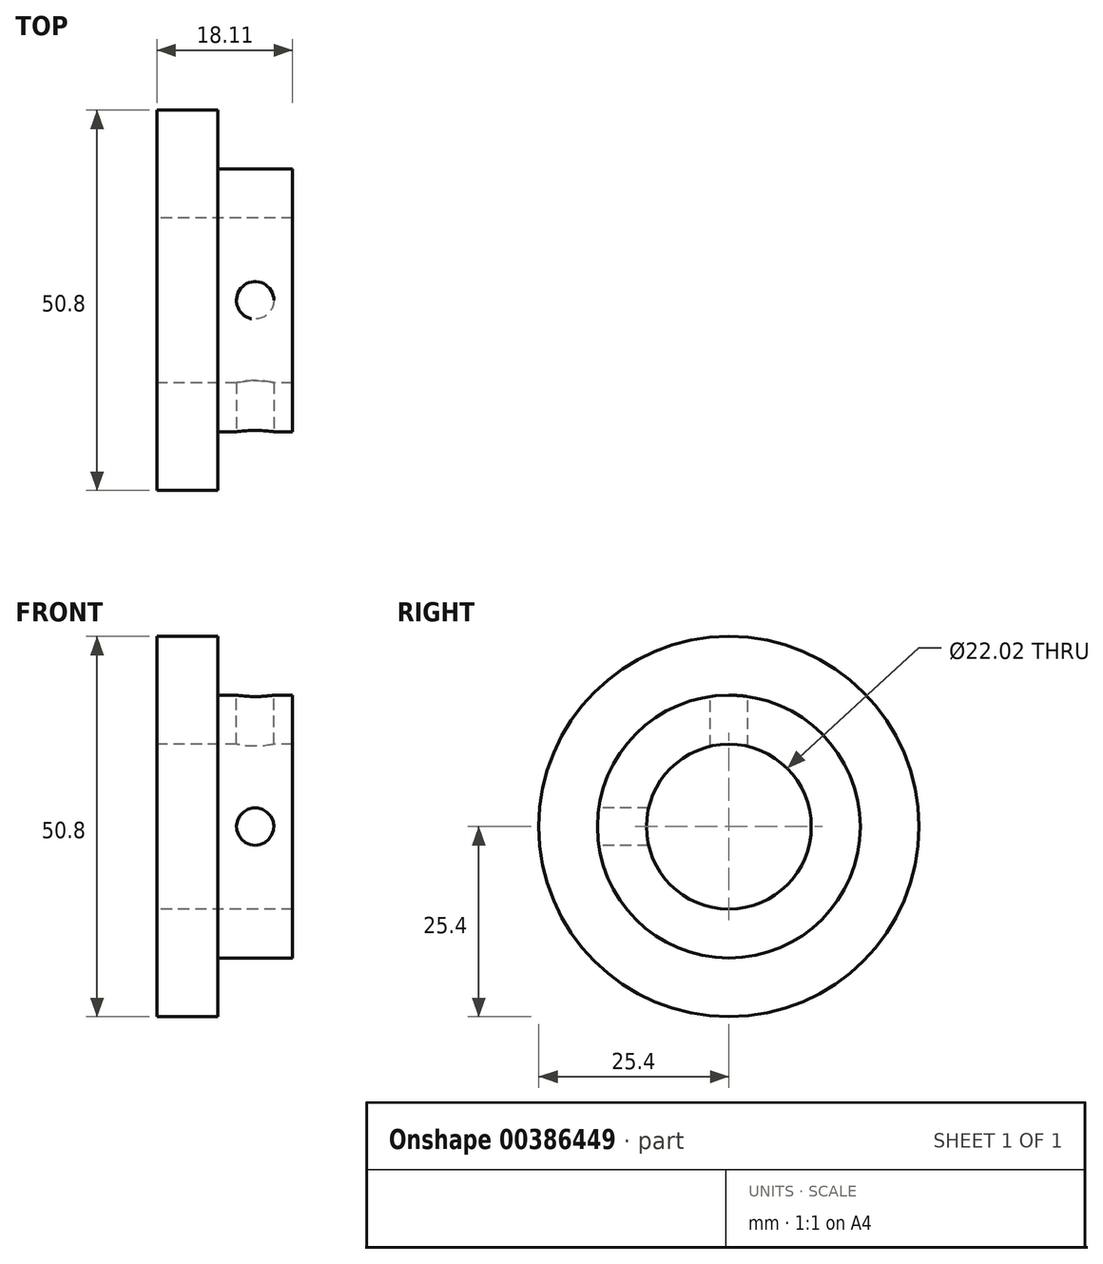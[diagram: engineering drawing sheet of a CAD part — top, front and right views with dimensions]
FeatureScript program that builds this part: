
annotation { "Feature Type Name" : "Feature", "Feature Type Description" : "" }
export const myFeature = defineFeature(function(context is Context, id is Id, definition is map)
    precondition{}
    {
        {
            var Q0;
            Q0=qCreatedBy(makeId("Front.planeOp"),FACE);
            var sketch = newSketch(context, id + "F0", { "sketchPlane" : qUnion([Q0])});
            skLineSegment(sketch, "E0", {"start": v(0, 0) * mm, "end": v(24.47, 0) * mm, "construction": true});
            skLineSegment(sketch, "E1", {"start": v(0, 11.01) * mm, "end": v(18.11, 11.01) * mm});
            skLineSegment(sketch, "E2", {"start": v(18.11, 11.01) * mm, "end": v(18.11, 17.55) * mm});
            skLineSegment(sketch, "E3", {"start": v(18.11, 17.55) * mm, "end": v(8.1, 17.55) * mm});
            skLineSegment(sketch, "E4", {"start": v(8.1, 17.55) * mm, "end": v(8.1, 25.4) * mm});
            skLineSegment(sketch, "E5", {"start": v(8.1, 25.4) * mm, "end": v(0, 25.4) * mm});
            skLineSegment(sketch, "E6", {"start": v(0, 25.4) * mm, "end": v(0, 11.01) * mm});
            skSolve(sketch);
        }
        {
            var Q0;
            Q0=makeQuery(id+"F0.imprint","IMPRINT",FACE,{"disambiguationData":[TD([[makeQuery(id+"F0.imprint","IMPRINT",EDGE,{"derivedFrom":sQuery(id+"F0.wireOp",EDGE,"E1")}),1.0]])]});
            var Q1;
            Q1=sQuery(id+"F0.wireOp",EDGE,"E0");
            revolve(context, id + "F1", {"entities" : qUnion([Q0]), "axis" : qUnion([Q1]), "revolveType" : RevolveType.FULL});
        }
        {
            var Q0;
            Q0=qCreatedBy(makeId("Front.planeOp"),FACE);
            cPlane(context, id + "F2", {"entities" : qUnion([Q0]), "cplaneType" : CPlaneType.OFFSET, "offset" : 17.55 * mm, "width" : 152.4 * mm, "height" : 152.4 * mm});
        }
        {
            var Q0;
            Q0=qCreatedBy(id+"F2.planeOp",FACE);
            var sketch = newSketch(context, id + "F3", { "sketchPlane" : qUnion([Q0])});
            skCircle(sketch, "E7", {"center": v(13.1, 0) * mm, "radius": 1.27 * mm});
            skSolve(sketch);
        }
        {
            var Q0;
            Q0=sQuery(id+"F3.wireOp",VERTEX,"E7.center");
            var Q1;
            Q1=makeQuery(id+"F1.opRevolve","SWEPT_BODY",BODY,{"disambiguationData":[OSD([sQuery(id+"F0.wireOp",EDGE,"E1"),sQuery(id+"F0.wireOp",EDGE,"E2"),sQuery(id+"F0.wireOp",EDGE,"E3"),sQuery(id+"F0.wireOp",EDGE,"E4"),sQuery(id+"F0.wireOp",EDGE,"E5"),sQuery(id+"F0.wireOp",EDGE,"E6")])]});
            hole(context, id + "F4", {"style" : HoleStyle.SIMPLE, "endStyle" : HoleEndStyle.BLIND, "standardTappedOrClearance" : lookupTablePath({ "standard" : "ISO", "engagement" : "75%", "pitch" : "1 mm", "size" : "M6", "type" : "Tapped" }), "standardBlindInLast" : lookupTablePath({ "standard" : "ISO", "engagement" : "75%", "pitch" : "1 mm", "size" : "M6", "type" : "Tapped" }), "holeDiameter" : 5 * mm, "showTappedDepth" : true, "holeDepth" : 11.06 * mm, "isTappedThrough" : true, "tappedDepth" : 8.06 * mm, "tapClearance" : 3, "startFromSketch" : true, "locations" : qUnion([Q0]), "scope" : qUnion([Q1]), "majorDiameter" : 6 * mm});
        }
        {
            var Q0;
            Q0=qCreatedBy(makeId("Top.planeOp"),FACE);
            cPlane(context, id + "F5", {"entities" : qUnion([Q0]), "cplaneType" : CPlaneType.OFFSET, "offset" : 17.55 * mm, "width" : 152.4 * mm, "height" : 152.4 * mm});
        }
        {
            var Q0;
            Q0=qCreatedBy(id+"F5.planeOp",FACE);
            var sketch = newSketch(context, id + "F6", { "sketchPlane" : qUnion([Q0])});
            skCircle(sketch, "E8", {"center": v(13.1, 0) * mm, "radius": 1.27 * mm});
            skSolve(sketch);
        }
        {
            var Q0;
            Q0=sQuery(id+"F6.wireOp",VERTEX,"E8.center");
            var Q1;
            Q1=makeQuery(id+"F1.opRevolve","SWEPT_BODY",BODY,{"disambiguationData":[OSD([sQuery(id+"F0.wireOp",EDGE,"E1"),sQuery(id+"F0.wireOp",EDGE,"E2"),sQuery(id+"F0.wireOp",EDGE,"E3"),sQuery(id+"F0.wireOp",EDGE,"E4"),sQuery(id+"F0.wireOp",EDGE,"E5"),sQuery(id+"F0.wireOp",EDGE,"E6")])]});
            hole(context, id + "F7", {"style" : HoleStyle.SIMPLE, "endStyle" : HoleEndStyle.BLIND, "standardTappedOrClearance" : lookupTablePath({ "standard" : "ISO", "engagement" : "75%", "pitch" : "1 mm", "size" : "M6", "type" : "Tapped" }), "standardBlindInLast" : lookupTablePath({ "standard" : "ISO", "engagement" : "75%", "pitch" : "1 mm", "size" : "M6", "type" : "Tapped" }), "holeDiameter" : 5 * mm, "showTappedDepth" : true, "holeDepth" : 11.06 * mm, "isTappedThrough" : true, "tappedDepth" : 8.06 * mm, "tapClearance" : 3, "startFromSketch" : true, "locations" : qUnion([Q0]), "scope" : qUnion([Q1]), "majorDiameter" : 6 * mm});
        }
    });
